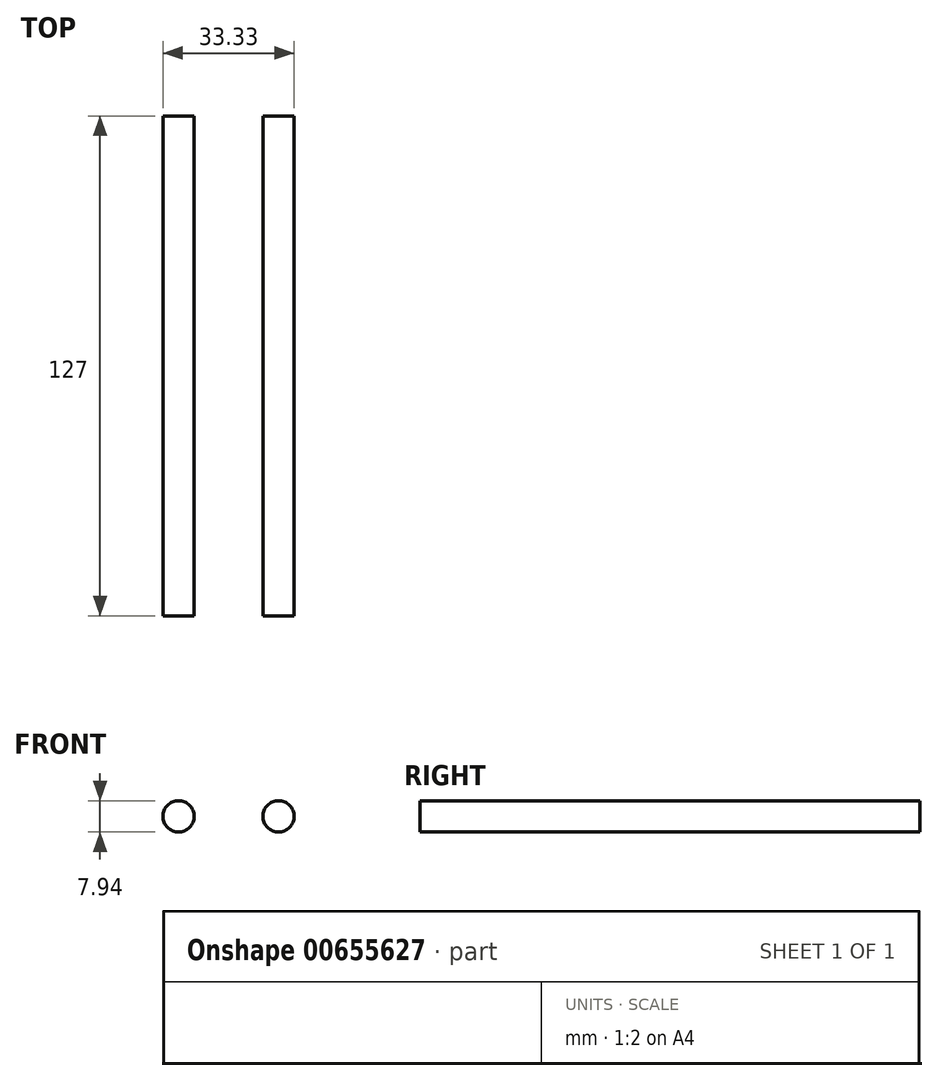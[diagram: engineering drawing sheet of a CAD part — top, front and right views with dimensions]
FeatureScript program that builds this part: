
annotation { "Feature Type Name" : "Feature", "Feature Type Description" : "" }
export const myFeature = defineFeature(function(context is Context, id is Id, definition is map)
    precondition{}
    {
        {
            var Q0;
            Q0=qCreatedBy(makeId("Front.planeOp"),FACE);
            var sketch = newSketch(context, id + "F0", { "sketchPlane" : qUnion([Q0])});
            skCircle(sketch, "E0", {"center": v(-34.53, 0) * mm, "radius": 3.97 * mm});
            skCircle(sketch, "E1", {"center": v(-9.13, 0) * mm, "radius": 3.97 * mm});
            skSolve(sketch);
        }
        {
            var Q0;
            Q0=makeQuery(id+"F0.imprint","IMPRINT",FACE,{"disambiguationData":[TD([[makeQuery(id+"F0.imprint","IMPRINT",EDGE,{"derivedFrom":sQuery(id+"F0.wireOp",EDGE,"E0")}),1.0]])]});
            var Q1;
            Q1=makeQuery(id+"F0.imprint","IMPRINT",FACE,{"disambiguationData":[TD([[makeQuery(id+"F0.imprint","IMPRINT",EDGE,{"derivedFrom":sQuery(id+"F0.wireOp",EDGE,"E1")}),1.0]])]});
            extrude(context, id + "F1", {"entities" : qUnion([Q0, Q1]), "depth" : 127 * mm, "offsetDistance" : 25.4 * mm});
        }
    });
